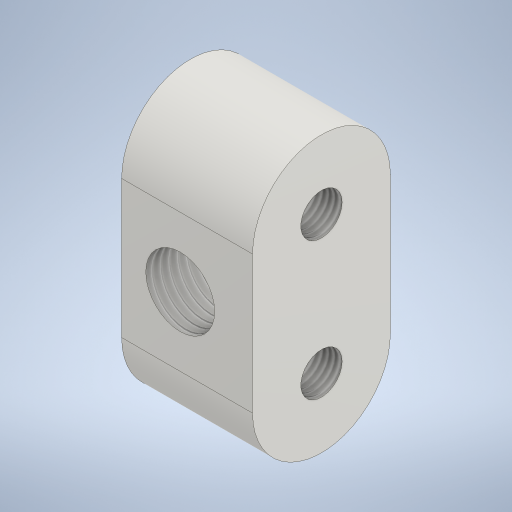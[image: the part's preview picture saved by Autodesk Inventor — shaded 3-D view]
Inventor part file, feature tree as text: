
AUTODESK INVENTOR PART (.ipt)
format: ipt  version: 2024 (Build 280153000, 153)  size: 291,328 bytes
history: native  units: mm
features: extrude x3, sketch x3, thread x3, other x2
ambient origin geometry x8: Origin, YZ Plane, XZ Plane, XY Plane, X Axis, Y Axis, Z Axis, Center Point
bodies: Body1 (feature_tree)
feature tree (11):
  extrude  "Extrusion2"  Depth=40.0mm
  other  "Full Round Fillet1"
  other  "Full Round Fillet2"
  sketch  "Sketch3"  dims[d12=80.0mm d13=40.0mm]
  sketch  "Sketch4"  dims[d14=20.0mm d15=20.0mm d16=17.0mm d17=12.0mm d18=12.0mm d19=42.0mm d20=0.0mm d21=42.0mm d22=0.0mm d29=40.0mm d30=0.0mm d31=40.0mm d32=20.0mm d37=350.0mm d38=0.0mm d39=350.0mm d40=0.0mm]
  extrude  "Extrusion3"  Depth=40.0mm
  extrude  "Extrusion4"  Depth=20.0mm
  thread  "Thread4"  [1 undecoded]
  thread  "Thread7"  [1 undecoded]
  thread  "Thread8"  [1 undecoded]
  sketch  "Sketch2"  dims[d9=38.0mm d10=0.0mm d11=40.0mm]
note: 3 required parameter values undecoded (feature->parameter linkage not recoverable at this tier; creation-order binding heuristic only, values carry confidence <= 0.55)
